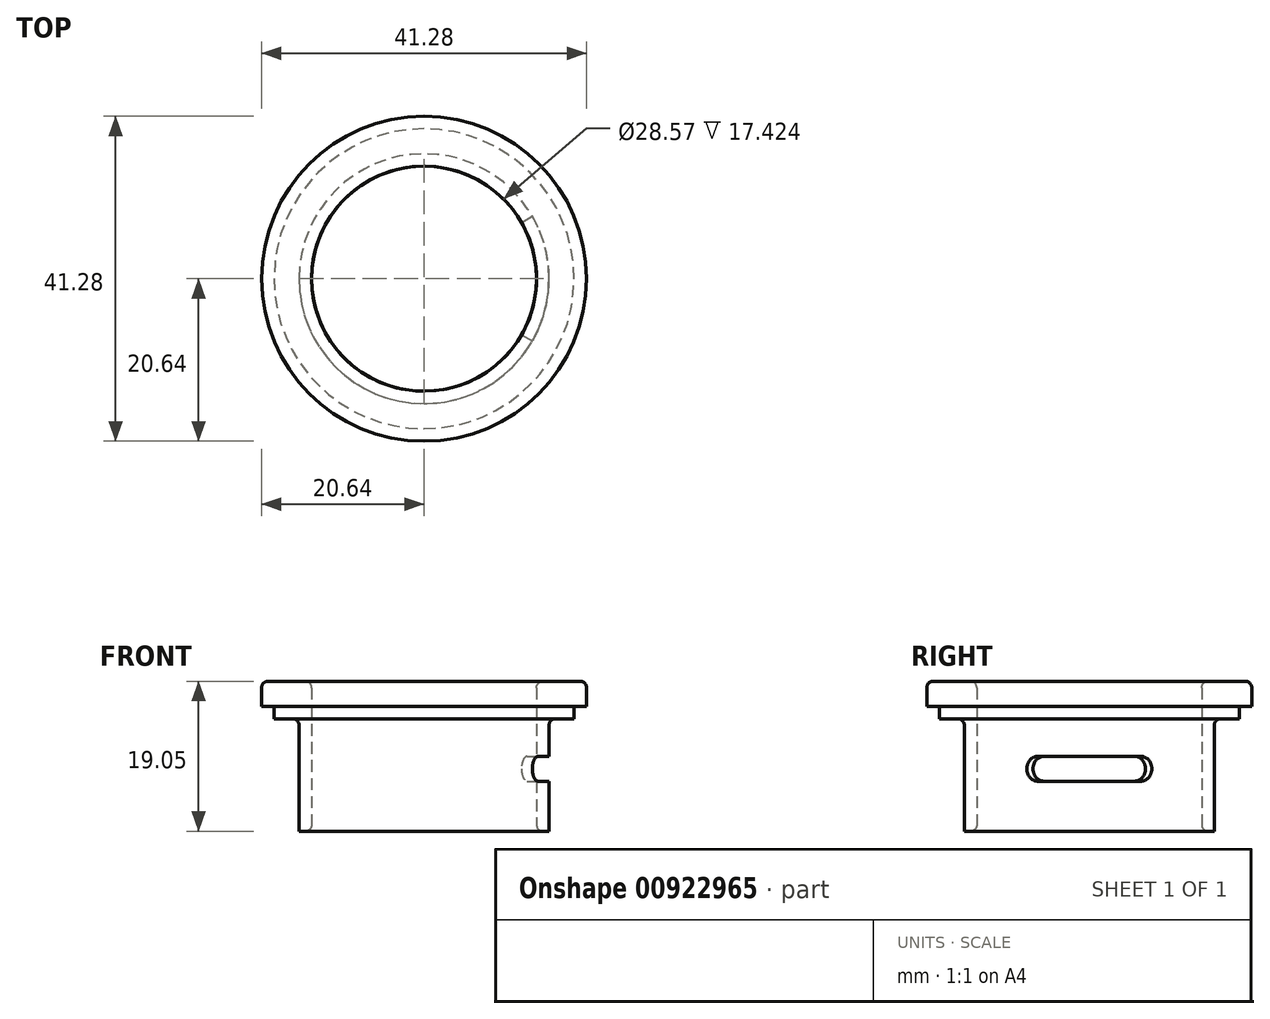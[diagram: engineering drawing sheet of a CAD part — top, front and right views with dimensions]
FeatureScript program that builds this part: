
annotation { "Feature Type Name" : "Feature", "Feature Type Description" : "" }
export const myFeature = defineFeature(function(context is Context, id is Id, definition is map)
    precondition{}
    {
        {
            var Q0;
            Q0=qCreatedBy(makeId("Front.planeOp"),FACE);
            var sketch = newSketch(context, id + "F0", { "sketchPlane" : qUnion([Q0])});
            skLineSegment(sketch, "E0", {"start": v(0, 0) * mm, "end": v(0, 71.51) * mm, "construction": true});
            skLineSegment(sketch, "E1", {"start": v(14.29, 0) * mm, "end": v(14.29, 19.05) * mm});
            skLineSegment(sketch, "E2", {"start": v(14.29, 19.05) * mm, "end": v(20.64, 19.05) * mm});
            skLineSegment(sketch, "E3", {"start": v(20.64, 19.05) * mm, "end": v(20.64, 15.87) * mm});
            skLineSegment(sketch, "E4", {"start": v(19.05, 14.29) * mm, "end": v(15.88, 14.29) * mm});
            skLineSegment(sketch, "E5", {"start": v(15.88, 14.29) * mm, "end": v(15.88, 0) * mm});
            skLineSegment(sketch, "E6", {"start": v(15.88, 0) * mm, "end": v(14.29, 0) * mm});
            skLineSegment(sketch, "E7", {"start": v(19.05, 14.29) * mm, "end": v(19.05, 15.87) * mm});
            skLineSegment(sketch, "E8", {"start": v(19.05, 15.87) * mm, "end": v(20.64, 15.87) * mm});
            skSolve(sketch);
        }
        {
            var Q0;
            Q0 = qSketchRegion(id + "F0", true);
            var Q1;
            Q1=sQuery(id+"F0.wireOp",EDGE,"E0");
            revolve(context, id + "F1", {"surfaceOperationType" : NewSurfaceOperationType.NEW, "entities" : qUnion([Q0]), "axis" : qUnion([Q1]), "revolveType" : RevolveType.FULL});
        }
        {
            var Q0;
            Q0=makeQuery(id+"F1.opRevolve","SWEPT_EDGE",EDGE,{"disambiguationData":[OSD([sQuery(id+"F0.wireOp",EDGE,"E1"),sQuery(id+"F0.wireOp",EDGE,"E2")])]});
            var Q1;
            Q1=makeQuery(id+"F1.opRevolve","SWEPT_EDGE",EDGE,{"disambiguationData":[OSD([sQuery(id+"F0.wireOp",EDGE,"E2"),sQuery(id+"F0.wireOp",EDGE,"E3")])]});
            var Q2;
            Q2=makeQuery(id+"F1.opRevolve","SWEPT_EDGE",EDGE,{"disambiguationData":[OSD([sQuery(id+"F0.wireOp",EDGE,"E4"),sQuery(id+"F0.wireOp",EDGE,"E5")])]});
            var Q3;
            Q3=makeQuery(id+"F1.opRevolve","SWEPT_EDGE",EDGE,{"disambiguationData":[OSD([sQuery(id+"F0.wireOp",EDGE,"E1"),sQuery(id+"F0.wireOp",EDGE,"E6")])]});
            fillet(context, id + "F2", {"entities" : qUnion([Q0, Q1, Q2, Q3]), "radius" : 0.81 * mm, "tangentPropagation" : true, "allowEdgeOverflow" : false});
        }
        {
            var Q0;
            Q0=makeQuery(id+"F1.opRevolve","SWEPT_FACE",FACE,{"disambiguationData":[OSD([sQuery(id+"F0.wireOp",EDGE,"E2")])]});
            cPlane(context, id + "F3", {"entities" : qUnion([Q0]), "cplaneType" : CPlaneType.OFFSET, "offset" : 12.7 * mm, "oppositeDirection" : true, "width" : 152.4 * mm, "height" : 152.4 * mm});
        }
        {
            var Q0;
            Q0=qCreatedBy(id+"F3.planeOp",FACE);
            var sketch = newSketch(context, id + "F4", { "sketchPlane" : qUnion([Q0])});
            skLineSegment(sketch, "E9", {"start": v(0, 0) * mm, "end": v(22, 12.7) * mm});
            skLineSegment(sketch, "E10", {"start": v(0, 0) * mm, "end": v(22, -12.7) * mm});
            skArc(sketch, "E11", {"start": v(22, -12.7) * mm, "mid": v(25.4, 0) * mm, "end": v(22, 12.7) * mm});
            skSolve(sketch);
        }
        {
            var Q0;
            Q0 = qSketchRegion(id + "F4", true);
            extrude(context, id + "F5", {"entities" : qUnion([Q0]), "operationType" : NewBodyOperationType.REMOVE, "depth" : 3.17 * mm, "offsetDistance" : 25.4 * mm});
        }
        {
            var Q0;
            Q0=makeQuery(id+"F5.boolean.opBoolean","COPY",EDGE,{"derivedFrom":makeQuery(id+"F5.opExtrude","CAP_EDGE",EDGE,{"disambiguationData":[OSD([sQuery(id+"F4.wireOp",EDGE,"E9")])],"isStart":true})});
            var Q1;
            Q1=makeQuery(id+"F5.boolean.opBoolean","COPY",EDGE,{"derivedFrom":makeQuery(id+"F5.opExtrude","CAP_EDGE",EDGE,{"disambiguationData":[OSD([sQuery(id+"F4.wireOp",EDGE,"E9")])],"isStart":false})});
            var Q2;
            Q2=makeQuery(id+"F5.boolean.opBoolean","COPY",EDGE,{"derivedFrom":makeQuery(id+"F5.opExtrude","CAP_EDGE",EDGE,{"disambiguationData":[OSD([sQuery(id+"F4.wireOp",EDGE,"E10")])],"isStart":true})});
            var Q3;
            Q3=makeQuery(id+"F5.boolean.opBoolean","COPY",EDGE,{"derivedFrom":makeQuery(id+"F5.opExtrude","CAP_EDGE",EDGE,{"disambiguationData":[OSD([sQuery(id+"F4.wireOp",EDGE,"E10")])],"isStart":false})});
            var Q4;
            Q4=makeQuery(id+"FYgGPzmfaGamFcG_1.3.F5.boolean.opBoolean","COPY",EDGE,{"derivedFrom":makeQuery(id+"FYgGPzmfaGamFcG_1.3.F5.opExtrude","CAP_EDGE",EDGE,{"disambiguationData":[OSD([sQuery(id+"F4.wireOp",EDGE,"E9")])],"isStart":false})});
            var Q5;
            Q5=makeQuery(id+"FYgGPzmfaGamFcG_1.3.F5.boolean.opBoolean","COPY",EDGE,{"derivedFrom":makeQuery(id+"FYgGPzmfaGamFcG_1.3.F5.opExtrude","CAP_EDGE",EDGE,{"disambiguationData":[OSD([sQuery(id+"F4.wireOp",EDGE,"E9")])],"isStart":true})});
            var Q6;
            Q6=makeQuery(id+"FYgGPzmfaGamFcG_1.1.F5.boolean.opBoolean","COPY",EDGE,{"derivedFrom":makeQuery(id+"FYgGPzmfaGamFcG_1.1.F5.opExtrude","CAP_EDGE",EDGE,{"disambiguationData":[OSD([sQuery(id+"F4.wireOp",EDGE,"E10")])],"isStart":false})});
            var Q7;
            Q7=makeQuery(id+"FYgGPzmfaGamFcG_1.1.F5.boolean.opBoolean","COPY",EDGE,{"derivedFrom":makeQuery(id+"FYgGPzmfaGamFcG_1.1.F5.opExtrude","CAP_EDGE",EDGE,{"disambiguationData":[OSD([sQuery(id+"F4.wireOp",EDGE,"E10")])],"isStart":true})});
            fillet(context, id + "F6", {"entities" : qUnion([Q0, Q1, Q2, Q3, Q4, Q5, Q6, Q7]), "radius" : 1.59 * mm, "tangentPropagation" : true, "allowEdgeOverflow" : false});
        }
    });
